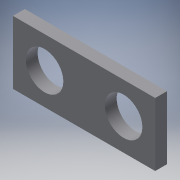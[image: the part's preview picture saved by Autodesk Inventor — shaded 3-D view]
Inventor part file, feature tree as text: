
AUTODESK INVENTOR PART (.ipt)
format: ipt  version: 2016 (Build 200138000, 138)  size: 97,792 bytes
history: native  units: in
note: dims shown in document units (in); Inventor stores cm internally (conversion verified against a paired STEP export)
features: extrude x1, sketch x1, reference x1
ambient origin geometry x8: Origin, YZ Plane, XZ Plane, XY Plane, X Axis, Y Axis, Z Axis, Center Point
bodies: Solid1 (feature_tree)
feature tree (3):
  extrude  "Extrusion1"  Depth=0.0591in
  sketch  "Sketch2"  dims[d0=0.187in d1=0.1575in d2=0.1575in d3=0.9055in d4=0.315in d5=0.0591in d6=0.0in]
  reference  "Reference1"
